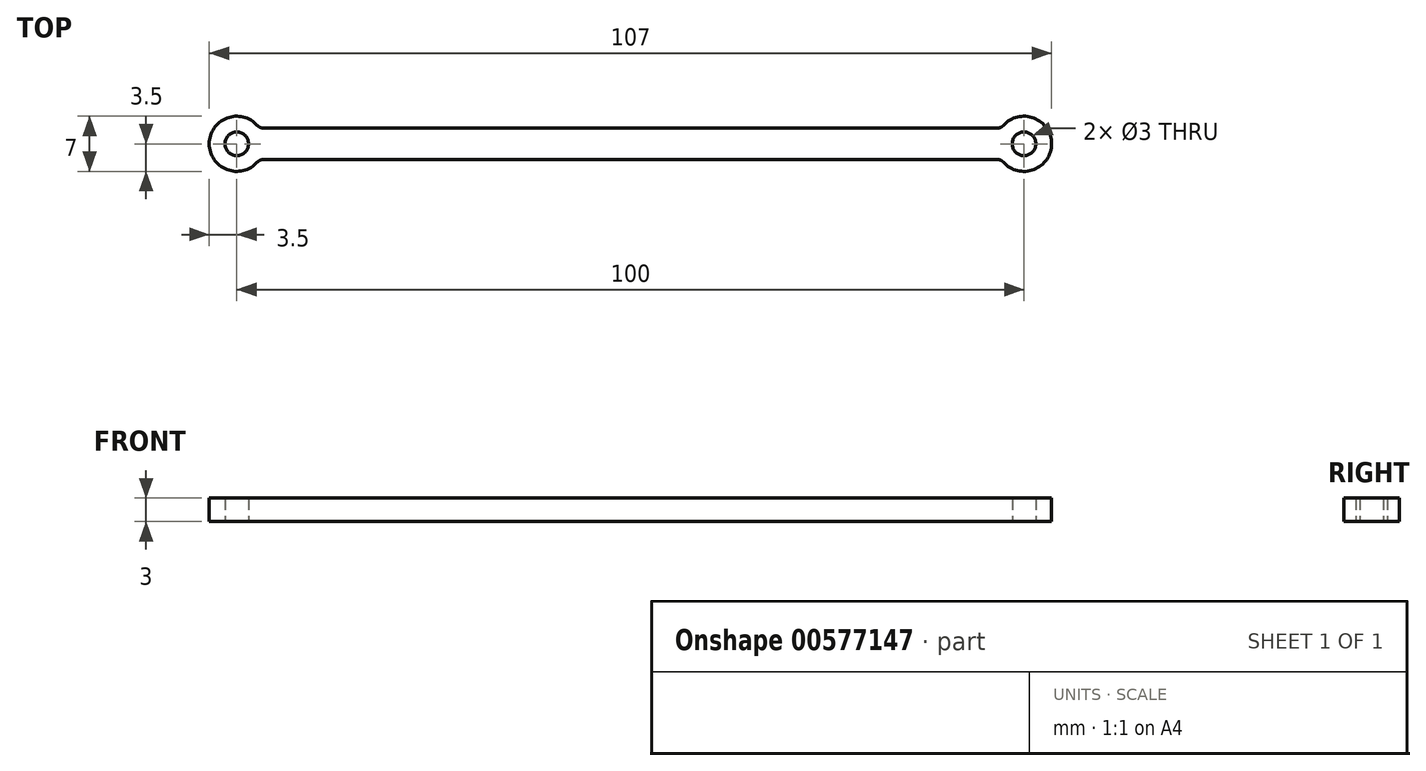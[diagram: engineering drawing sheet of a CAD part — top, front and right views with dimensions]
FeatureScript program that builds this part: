
annotation { "Feature Type Name" : "Feature", "Feature Type Description" : "" }
export const myFeature = defineFeature(function(context is Context, id is Id, definition is map)
    precondition{}
    {
        {
            var Q0;
            Q0=qCreatedBy(makeId("Top.planeOp"),FACE);
            var sketch = newSketch(context, id + "F0", { "sketchPlane" : qUnion([Q0])});
            skCircle(sketch, "E0", {"center": v(-50, 0) * mm, "radius": 1.5 * mm});
            skArc(sketch, "E1.0", {"start": v(-47.4, 2.33) * mm, "mid": v(-53.5, 0) * mm, "end": v(-47.4, -2.33) * mm});
            skLineSegment(sketch, "E2", {"start": v(-46.65, 2) * mm, "end": v(0, 2) * mm});
            skLineSegment(sketch, "E3", {"start": v(0, -2) * mm, "end": v(-46.65, -2) * mm});
            skPoint(sketch, "E4.visualSharp", {"position": v(-47.13, 2) * mm});
            skArc(sketch, "E4.filletArc", {"start": v(-47.4, 2.33) * mm, "mid": v(-47.05, 2.09) * mm, "end": v(-46.65, 2) * mm});
            skPoint(sketch, "E5.visualSharp", {"position": v(-47.13, -2) * mm});
            skArc(sketch, "E5.filletArc", {"start": v(-46.65, -2) * mm, "mid": v(-47.05, -2.09) * mm, "end": v(-47.4, -2.33) * mm});
            skLineSegment(sketch, "E6.MirrorCS", {"start": v(46.65, 2) * mm, "end": v(0, 2) * mm});
            skLineSegment(sketch, "E7.MirrorCS", {"start": v(0, -2) * mm, "end": v(46.65, -2) * mm});
            skArc(sketch, "E8.MirrorCS", {"start": v(46.65, -2) * mm, "mid": v(47.05, -2.09) * mm, "end": v(47.4, -2.33) * mm});
            skCircle(sketch, "E9.MirrorC", {"center": v(50, 0) * mm, "radius": 1.5 * mm});
            skArc(sketch, "E10.MirrorCS", {"start": v(47.4, 2.33) * mm, "mid": v(53.5, 0) * mm, "end": v(47.4, -2.33) * mm});
            skArc(sketch, "E11.MirrorCS", {"start": v(47.4, 2.33) * mm, "mid": v(47.05, 2.09) * mm, "end": v(46.65, 2) * mm});
            skSolve(sketch);
        }
        {
            var Q0;
            Q0=qSketchRegion(id+"F0",true);
            extrude(context, id + "F1", {"entities" : qUnion([Q0]), "endBound" : BoundingType.SYMMETRIC, "depth" : 3 * mm});
        }
    });
